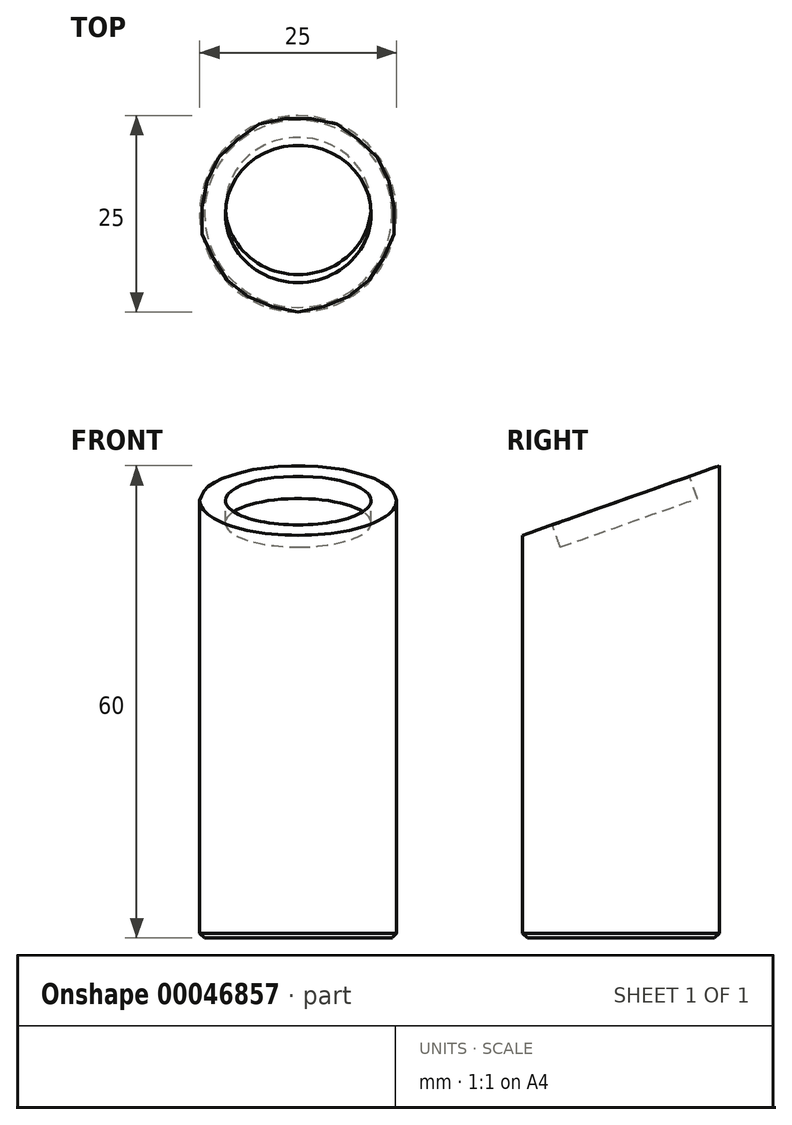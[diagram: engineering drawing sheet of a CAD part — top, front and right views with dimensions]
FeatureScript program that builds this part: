
annotation { "Feature Type Name" : "Feature", "Feature Type Description" : "" }
export const myFeature = defineFeature(function(context is Context, id is Id, definition is map)
    precondition{}
    {
        {
            var Q0;
            Q0=qCreatedBy(makeId("Top.planeOp"),FACE);
            var sketch = newSketch(context, id + "F0", { "sketchPlane" : qUnion([Q0])});
            skCircle(sketch, "E0", {"center": v(0, 0) * mm, "radius": 12.5 * mm});
            skSolve(sketch);
        }
        {
            var Q0;
            Q0 = qSketchRegion(id + "F0", true);
            extrude(context, id + "F1", {"entities" : qUnion([Q0]), "depth" : 60 * mm});
        }
        {
            var Q0;
            Q0=qCreatedBy(makeId("Right.planeOp"),FACE);
            var sketch = newSketch(context, id + "F2", { "sketchPlane" : qUnion([Q0])});
            skLineSegment(sketch, "E1.0", {"start": v(-12.5, 60) * mm, "end": v(12.5, 60) * mm});
            skLineSegment(sketch, "E2", {"start": v(12.5, 60) * mm, "end": v(-12.5, 51.16) * mm});
            skLineSegment(sketch, "E3", {"start": v(-12.5, 51.16) * mm, "end": v(-12.5, 60) * mm});
            skSolve(sketch);
        }
        {
            var Q0;
            Q0=makeQuery(id+"F2.imprint","IMPRINT",FACE,{"disambiguationData":[TD([[makeQuery(id+"F2.imprint","IMPRINT",EDGE,{"derivedFrom":sQuery(id+"F2.wireOp",EDGE,"E1.0")}),-1.0]])]});
            extrude(context, id + "F3", {"entities" : qUnion([Q0]), "operationType" : NewBodyOperationType.REMOVE, "endBound" : BoundingType.UP_TO_NEXT, "oppositeDirection" : true, "depth" : 25 * mm, "hasSecondDirection" : true, "secondDirectionBound" : SecondDirectionBoundingType.UP_TO_NEXT, "secondDirectionOppositeDirection" : false, "secondDirectionDepth" : 25 * mm});
        }
        {
            var Q0;
            Q0=makeQuery(id+"F3.boolean.opBoolean","COPY",FACE,{"derivedFrom":makeQuery(id+"F3.opExtrude","SWEPT_FACE",FACE,{"disambiguationData":[OSD([sQuery(id+"F2.wireOp",EDGE,"E2")])]})});
            var sketch = newSketch(context, id + "F4", { "sketchPlane" : qUnion([Q0])});
            skCircle(sketch, "E4", {"center": v(0, 18.53) * mm, "radius": 9.25 * mm});
            skSolve(sketch);
        }
        {
            var Q0;
            Q0 = qSketchRegion(id + "F4", true);
            extrude(context, id + "F5", {"entities" : qUnion([Q0]), "operationType" : NewBodyOperationType.REMOVE, "oppositeDirection" : true, "depth" : 3 * mm});
        }
        {
            var Q0;
            Q0=makeQuery(id+"F1.opExtrude","CAP_FACE",FACE,{"disambiguationData":[OSD([sQuery(id+"F0.wireOp",EDGE,"E0")])],"isStart":true});
            chamfer(context, id + "F6", {"entities" : qUnion([Q0]), "width" : .6 * mm, "tangentPropagation" : true});
        }
    });
